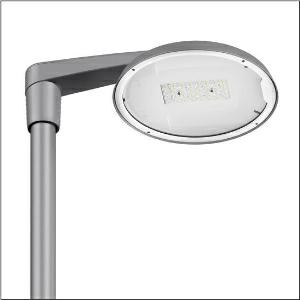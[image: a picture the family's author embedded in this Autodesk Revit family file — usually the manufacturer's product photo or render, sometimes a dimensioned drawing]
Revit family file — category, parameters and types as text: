
# Revit family: dl_r__50_iq_mini___st0_5a_5xa248b31f08ke_5f87
name_source: partatom
category: Lighting Fixtures
units: mm (PartAtom-declared; Revit-internal decimal feet)

## family parameters
Cut with Voids When Loaded = No
Host = Face
Light Source = No
Part Type = Normal
Room Calculation Point = No
Round Connector Dimension = Use Diameter
Shared = No

## types (1)
- --- (1 x LED, 5500 lm, 32.1 W, 3000K)
    Apparent Load = 32 VA
    CIE Flux Codes = 43 76 97 100 100
    Color Rendering = 70
    Color Temperature = 3000K
    Default Elevation = 1800 mm
    Description = DL® 50 iQ mini, mast luminaire, primary light control with lens, of PMMA, primary optical cover: cover, of toughened safety glass, transparent, light distribution: ST0.5a, light emission: direct distribution, primary light characteristic: asymmetric, installation type: side-entry, post-top, LED, High Power LED, rated luminous flux: 5.500lm, luminous efficacy: 171lm/W, light colour: 730, colour temperature: 3000K, control: optimised constant luminous flux control (CLO 2.0), Desk-Remote (wireless, voltage-free reading and setting of iQ features in the workshop via application-optimized NFC function/RFID function), Light-Fading, Smart-Wire, Night-Set, Lumen-Switch, Temp-Guard, Auto-Match, Street-Remote, mains connection: 230..240V, AC, 50/60Hz, connection cable pre-assembled, cable length: 6,5m, start of lifetime: 32W, end of service life: 33W, reduction: 16W, luminaire housing, of diecast aluminium, powder-coated, Siteco® metallic grey (DB 702S), inclination adjustable: 0°, 5°, 10° (post-top) | 0°, -5°, -10°, -15° (side-entry), please order mast post-top element or mast side-entry element separately, diameter: 500mm, height: 115mm, post-top: for spigot size d x l = 76 x 100mm; with reducer (optional accessory) 60 x 100mm | side-entry: for spigot size d x l = 60 x 100mm; with reducer (optional accessory) 42 x 100mm, protection rating (complete): IP66, insulation class (complete): insulation class II (safety insulation), certification: CE, ENEC, VDE, impact resistance: IK08, permissible operating ambient temperature for outdoor applications: -25..+40°C, standard-compliant lighting for roads and squares, packaging unit: 1 piece

Light Distribution: ST0.5a
    Height = 115 mm
    Lamp = 1 x LED
    Lamp Light Flux = 5500 lm
    Lamp Power = 32.1 W
    Lamp count = 1
    Length = 500 mm
    Luminous efficacy = 171 lm/W
    Manufacturer = Siteco
    ModVariant = No
    Model = 5XA248B31F08KE
    Number of Poles = 1
    OnlyDefault = Yes
    Power Factor = 1
    Product Name = DL® 50 iQ mini | ST0.5a
    Product group = mast luminaire | pylon top
    ProductGroupID = 6100
    Protection Class = Protection class II
    Protection Degree = IP 66
    RLX_Detail_Level = 1
    RLX_Emergency_Light_Flux = 0 lm
    RLX_Emergency_Type = 0
    RLX_Emergency_Type_DB = No
    RlxData = <blob elided: 126957 chars, md5=bd1e4c60>
    Socket = socket
    Standby Power = 0 W
    System Light Flux = 5500 lm
    System Power = 32 W
    Type Comments = factory setting: luminous flux: 100 % | dim-lin: 254 | 343 mA
    Type Image = l_1251794.jpg
    URL = http://relux.com
    VarID = @adj_092365
    Voltage = 0 V
    Weight = 0.00 kg
    Width = 0 mm  [stored 0 ft]

note: [stored X ft] marks values corroborated as IEEE doubles in the binary element streams (Revit-internal decimal feet)

## geometry (parser evidence)
native form markers: Blend x4, Sweep x12
no freeform markers — native parametric forms only
